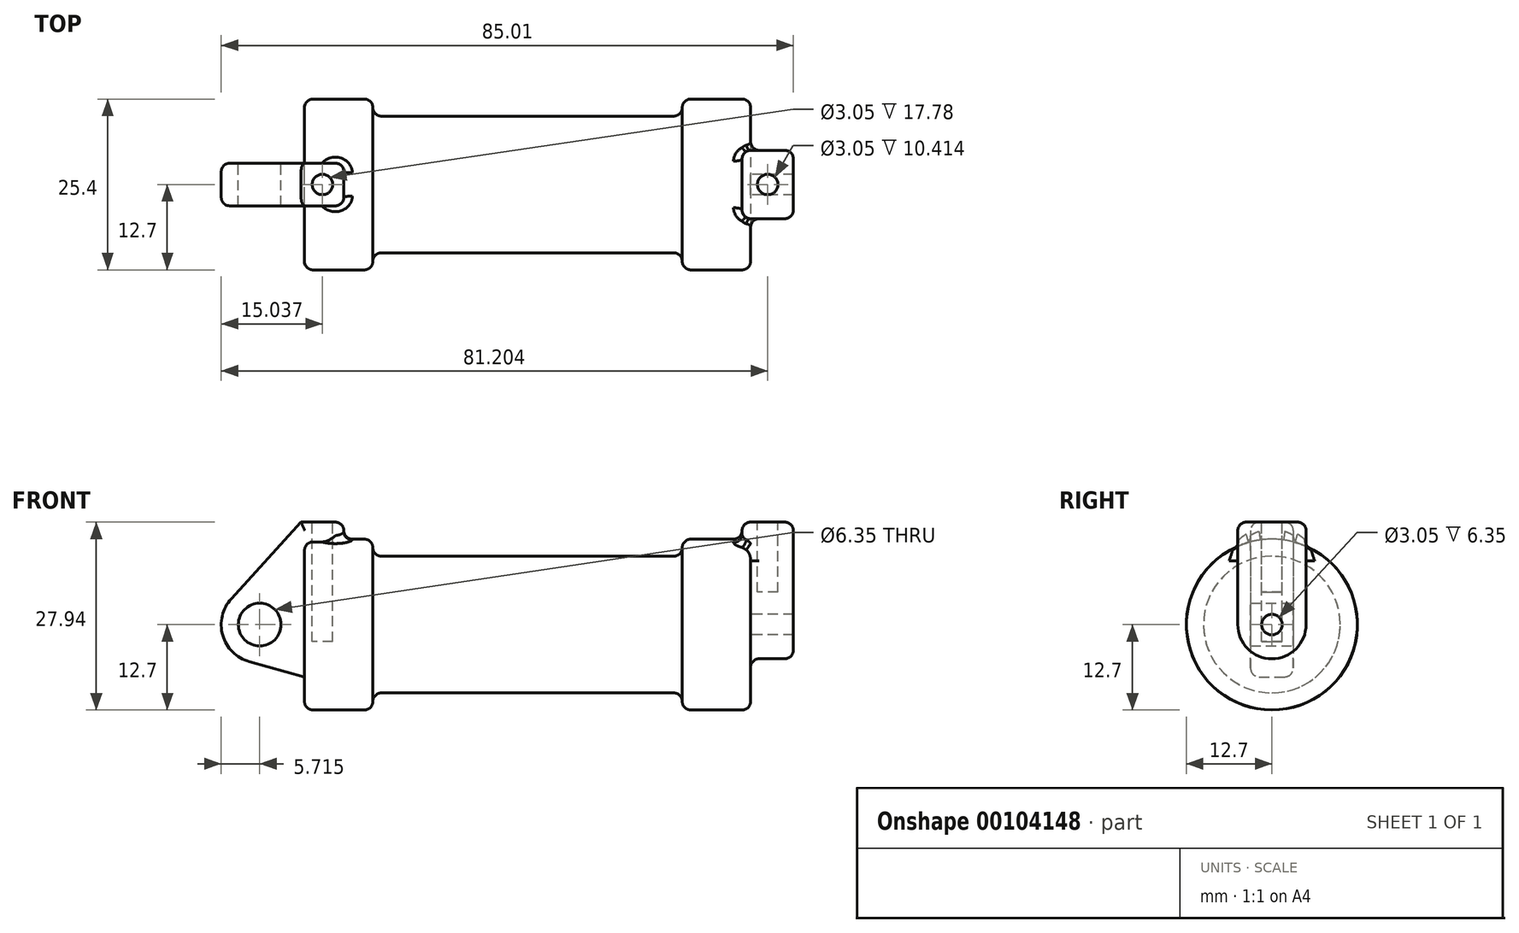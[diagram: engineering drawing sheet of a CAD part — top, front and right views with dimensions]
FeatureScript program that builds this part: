
annotation { "Feature Type Name" : "Feature", "Feature Type Description" : "" }
export const myFeature = defineFeature(function(context is Context, id is Id, definition is map)
    precondition{}
    {
        {
            var Q0;
            Q0=qCreatedBy(makeId("Front.planeOp"),FACE);
            var sketch = newSketch(context, id + "F0", { "sketchPlane" : qUnion([Q0])});
            skLineSegment(sketch, "E0", {"start": v(0, 0) * mm, "end": v(0, 12.7) * mm});
            skLineSegment(sketch, "E1", {"start": v(0, 12.7) * mm, "end": v(10.16, 12.7) * mm});
            skLineSegment(sketch, "E2", {"start": v(10.16, 12.7) * mm, "end": v(10.16, 10.16) * mm});
            skLineSegment(sketch, "E3", {"start": v(10.16, 10.16) * mm, "end": v(56.13, 10.16) * mm});
            skLineSegment(sketch, "E4", {"start": v(56.13, 10.16) * mm, "end": v(56.13, 12.7) * mm});
            skLineSegment(sketch, "E5", {"start": v(56.13, 12.7) * mm, "end": v(66.3, 12.7) * mm});
            skLineSegment(sketch, "E6", {"start": v(66.3, 12.7) * mm, "end": v(66.3, 0) * mm});
            skLineSegment(sketch, "E7", {"start": v(66.3, 0) * mm, "end": v(0, 0) * mm});
            skLineSegment(sketch, "E8", {"start": v(5.84, 15.24) * mm, "end": v(-0.5, 15.24) * mm});
            skLineSegment(sketch, "E9", {"start": v(-0.5, 15.24) * mm, "end": v(-10.88, 3.85) * mm});
            skLineSegment(sketch, "E10", {"start": v(0, 0) * mm, "end": v(-6.65, 0) * mm});
            skCircle(sketch, "E11", {"center": v(-6.65, 0) * mm, "radius": 5.72 * mm});
            skCircle(sketch, "E12", {"center": v(-6.65, 0) * mm, "radius": 3.18 * mm});
            skLineSegment(sketch, "E13", {"start": v(5.84, 15.24) * mm, "end": v(5.84, -9.4) * mm});
            skLineSegment(sketch, "E14", {"start": v(5.84, -9.4) * mm, "end": v(-8.18, -5.5) * mm});
            skSolve(sketch);
        }
        {
            var Q0;
            {var subQ0=sQuery(id+"F0.wireOp",EDGE,"E2");Q0=makeQuery(id+"F0.imprint","IMPRINT",FACE,{"disambiguationData":[TD([[makeQuery(id+"F0.imprint","IMPRINT",EDGE,{"derivedFrom":subQ0}),-1.0]])]});}
            var Q1;
            {var subQ0=sQuery(id+"F0.wireOp",EDGE,"E0");Q1=makeQuery(id+"F0.imprint","IMPRINT",FACE,{"disambiguationData":[TD([[makeQuery(id+"F0.imprint","IMPRINT",EDGE,{"derivedFrom":subQ0}),-1.0]])]});}
            var Q2;
            Q2=sQuery(id+"F0.wireOp",EDGE,"E7");
            revolve(context, id + "F1", {"entities" : qUnion([Q0, Q1]), "axis" : qUnion([Q2]), "revolveType" : RevolveType.FULL});
        }
        {
            var Q0;
            {var subQ0=sQuery(id+"F0.wireOp",EDGE,"E0");Q0=makeQuery(id+"F0.imprint","IMPRINT",FACE,{"disambiguationData":[TD([[makeQuery(id+"F0.imprint","IMPRINT",EDGE,{"derivedFrom":subQ0}),-1.0]])]});}
            var Q1;
            {var subQ3=sQuery(id+"F0.wireOp",EDGE,"E0");Q1=makeQuery(id+"F0.imprint","IMPRINT",FACE,{"disambiguationData":[TD([[makeQuery(id+"F0.imprint","IMPRINT",EDGE,{"derivedFrom":subQ3}),1.0]])]});}
            var Q2;
            {var subQ4=sQuery(id+"F0.wireOp",EDGE,"E12");Q2=makeQuery(id+"F0.imprint","IMPRINT",FACE,{"disambiguationData":[TD([[makeQuery(id+"F0.imprint","IMPRINT",EDGE,{"derivedFrom":subQ4}),-1.0]])]});}
            var Q3;
            {var subQ0=sQuery(id+"F0.wireOp",EDGE,"E14");Q3=makeQuery(id+"F0.imprint","IMPRINT",FACE,{"disambiguationData":[TD([[makeQuery(id+"F0.imprint","IMPRINT",EDGE,{"derivedFrom":subQ0}),-1.0]])]});}
            extrude(context, id + "F2", {"entities" : qUnion([Q0, Q1, Q2, Q3]), "operationType" : NewBodyOperationType.ADD, "endBound" : BoundingType.SYMMETRIC, "depth" : 6.35 * mm});
        }
        {
            var Q0;
            Q0=makeQuery(id+"F1.opRevolve","SWEPT_FACE",FACE,{"disambiguationData":[OSD([sQuery(id+"F0.wireOp",EDGE,"E6")])]});
            var sketch = newSketch(context, id + "F3", { "sketchPlane" : qUnion([Q0])});
            skCircle(sketch, "E15", {"center": v(0, 0) * mm, "radius": 1.52 * mm});
            skCircle(sketch, "E16", {"center": v(0, 0) * mm, "radius": 5.08 * mm});
            skLineSegment(sketch, "E17", {"start": v(5.08, 0) * mm, "end": v(5.08, 15.24) * mm});
            skLineSegment(sketch, "E18", {"start": v(-5.08, 0) * mm, "end": v(-5.08, 15.24) * mm});
            skLineSegment(sketch, "E19", {"start": v(-5.08, 15.24) * mm, "end": v(5.08, 15.24) * mm});
            skSolve(sketch);
        }
        {
            var Q0;
            Q0 = qSketchRegion(id + "F3", true);
            extrude(context, id + "F4", {"entities" : qUnion([Q0]), "operationType" : NewBodyOperationType.ADD, "depth" : 6.35 * mm});
        }
        {
            var Q0;
            Q0 = qSketchRegion(id + "F3", true);
            extrude(context, id + "F5", {"entities" : qUnion([Q0]), "operationType" : NewBodyOperationType.ADD, "oppositeDirection" : true, "depth" : 1.27 * mm});
        }
        {
            var Q0;
            {var subQ0=sQuery(id+"F3.wireOp",EDGE,"E19");Q0=makeQuery(id+"F5.boolean.opBoolean","MERGE",FACE,{"derivedFrom":[makeQuery(id+"F4.opExtrude","SWEPT_FACE",FACE,{"disambiguationData":[OSD([subQ0])]}),makeQuery(id+"F5.opExtrude","SWEPT_FACE",FACE,{"disambiguationData":[OSD([subQ0])]})]});}
            var sketch = newSketch(context, id + "F6", { "sketchPlane" : qUnion([Q0])});
            skCircle(sketch, "E20", {"center": v(68.83, 0) * mm, "radius": 1.52 * mm});
            skLineSegment(sketch, "E21", {"start": v(68.83, 5.08) * mm, "end": v(68.83, 1.52) * mm});
            skLineSegment(sketch, "E22", {"start": v(65.02, 0) * mm, "end": v(67.31, 0) * mm});
            skLineSegment(sketch, "E23.trimOffspring", {"start": v(68.83, -1.52) * mm, "end": v(68.83, -5.08) * mm});
            skLineSegment(sketch, "E24.trimOffspring", {"start": v(70.36, 0) * mm, "end": v(72.64, 0) * mm});
            skSolve(sketch);
        }
        {
            var Q0;
            Q0=makeQuery(id+"F2.opExtrude","SWEPT_FACE",FACE,{"disambiguationData":[OSD([sQuery(id+"F0.wireOp",EDGE,"E8")])]});
            var sketch = newSketch(context, id + "F7", { "sketchPlane" : qUnion([Q0])});
            skCircle(sketch, "E25", {"center": v(2.67, 0) * mm, "radius": 1.52 * mm});
            skLineSegment(sketch, "E26", {"start": v(5.84, 0) * mm, "end": v(4.2, 0) * mm});
            skLineSegment(sketch, "E27", {"start": v(2.67, 3.18) * mm, "end": v(2.67, 1.52) * mm});
            skLineSegment(sketch, "E28.trimOffspring", {"start": v(2.67, -1.52) * mm, "end": v(2.67, -3.18) * mm});
            skLineSegment(sketch, "E29.trimOffspring", {"start": v(1.14, 0) * mm, "end": v(-0.5, 0) * mm});
            skSolve(sketch);
        }
        {
            var Q0;
            {var subQ0=sQuery(id+"F7.wireOp",EDGE,"E25");var subQ1=makeQuery(id+"F7.imprint","INTERSECT",VERTEX,{"derivedFrom":[subQ0,sQuery(id+"F7.wireOp",EDGE,"E26")]});Q0=makeQuery(id+"F7.imprint","IMPRINT",FACE,{"disambiguationData":[TD([[makeQuery(id+"F7.imprint","IMPRINT",EDGE,{"disambiguationData":[TD([[subQ1,-1.0]])],"derivedFrom":subQ0}),1.0]])]});}
            extrude(context, id + "F8", {"entities" : qUnion([Q0]), "operationType" : NewBodyOperationType.REMOVE, "oppositeDirection" : true, "depth" : 17.78 * mm});
        }
        {
            var Q0;
            {var subQ0=sQuery(id+"F6.wireOp",EDGE,"E20");var subQ1=makeQuery(id+"F6.imprint","INTERSECT",VERTEX,{"derivedFrom":[subQ0,sQuery(id+"F6.wireOp",EDGE,"E21")]});Q0=makeQuery(id+"F6.imprint","IMPRINT",FACE,{"disambiguationData":[TD([[makeQuery(id+"F6.imprint","IMPRINT",EDGE,{"disambiguationData":[TD([[subQ1,1.0]])],"derivedFrom":subQ0}),1.0]])]});}
            extrude(context, id + "F9", {"entities" : qUnion([Q0]), "operationType" : NewBodyOperationType.REMOVE, "oppositeDirection" : true, "depth" : 10.4 * mm});
        }
        {
            var Q0;
            Q0=makeQuery(id+"F1.opRevolve","SWEPT_EDGE",EDGE,{"disambiguationData":[OSD([sQuery(id+"F0.wireOp",EDGE,"E1"),sQuery(id+"F0.wireOp",EDGE,"E2")])]});
            var Q1;
            Q1=makeQuery(id+"F1.opRevolve","SWEPT_EDGE",EDGE,{"disambiguationData":[OSD([sQuery(id+"F0.wireOp",EDGE,"E0"),sQuery(id+"F0.wireOp",EDGE,"E1")])]});
            var Q2;
            Q2=makeQuery(id+"F4.boolean.opBoolean","SPLIT",EDGE,{"disambiguationData":[OD(1.0)],"derivedFrom":makeQuery(id+"F1.opRevolve","SWEPT_EDGE",EDGE,{"disambiguationData":[OSD([sQuery(id+"F0.wireOp",EDGE,"E5"),sQuery(id+"F0.wireOp",EDGE,"E6")])]})});
            var Q3;
            Q3=makeQuery(id+"F1.opRevolve","SWEPT_EDGE",EDGE,{"disambiguationData":[OSD([sQuery(id+"F0.wireOp",EDGE,"E4"),sQuery(id+"F0.wireOp",EDGE,"E5")])]});
            var Q4;
            Q4=makeQuery(id+"F1.opRevolve","SWEPT_EDGE",EDGE,{"disambiguationData":[OSD([sQuery(id+"F0.wireOp",EDGE,"E2"),sQuery(id+"F0.wireOp",EDGE,"E3")])]});
            var Q5;
            Q5=makeQuery(id+"F1.opRevolve","SWEPT_EDGE",EDGE,{"disambiguationData":[OSD([sQuery(id+"F0.wireOp",EDGE,"E3"),sQuery(id+"F0.wireOp",EDGE,"E4")])]});
            fillet(context, id + "F10", {"entities" : qUnion([Q0, Q1, Q2, Q3, Q4, Q5]), "radius" : 1.27 * mm, "tangentPropagation" : true, "allowEdgeOverflow" : false});
        }
        {
            var Q0;
            Q0=makeQuery(id+"F2.opExtrude","CAP_EDGE",EDGE,{"disambiguationData":[OSD([sQuery(id+"F0.wireOp",EDGE,"E9")])],"isStart":false});
            var Q1;
            Q1=makeQuery(id+"F2.opExtrude","CAP_EDGE",EDGE,{"disambiguationData":[OSD([sQuery(id+"F0.wireOp",EDGE,"E9")])],"isStart":true});
            var Q2;
            Q2=makeQuery(id+"F2.opExtrude","CAP_EDGE",EDGE,{"disambiguationData":[OSD([sQuery(id+"F0.wireOp",EDGE,"E8")])],"isStart":true});
            var Q3;
            Q3=makeQuery(id+"F2.opExtrude","CAP_EDGE",EDGE,{"disambiguationData":[OSD([sQuery(id+"F0.wireOp",EDGE,"E8")])],"isStart":false});
            var Q4;
            Q4=makeQuery(id+"F2.opExtrude","CAP_EDGE",EDGE,{"disambiguationData":[OSD([sQuery(id+"F0.wireOp",EDGE,"E13")])],"isStart":false});
            var Q5;
            Q5=makeQuery(id+"F2.opExtrude","SWEPT_EDGE",EDGE,{"disambiguationData":[OSD([sQuery(id+"F0.wireOp",EDGE,"E8"),sQuery(id+"F0.wireOp",EDGE,"E13")])]});
            var Q6;
            Q6=makeQuery(id+"F2.opExtrude","CAP_EDGE",EDGE,{"disambiguationData":[OSD([sQuery(id+"F0.wireOp",EDGE,"E13")])],"isStart":true});
            var Q7;
            Q7=makeQuery(id+"F2.opExtrude","CAP_EDGE",EDGE,{"disambiguationData":[OSD([sQuery(id+"F0.wireOp",EDGE,"E11")])],"isStart":false});
            var Q8;
            Q8=makeQuery(id+"F2.opExtrude","CAP_EDGE",EDGE,{"disambiguationData":[OSD([sQuery(id+"F0.wireOp",EDGE,"E14")])],"isStart":false});
            var Q9;
            Q9=makeQuery(id+"F2.opExtrude","CAP_EDGE",EDGE,{"disambiguationData":[OSD([sQuery(id+"F0.wireOp",EDGE,"E14")])],"isStart":true});
            var Q10;
            Q10=makeQuery(id+"F2.opExtrude","CAP_EDGE",EDGE,{"disambiguationData":[OSD([sQuery(id+"F0.wireOp",EDGE,"E11")])],"isStart":true});
            var Q11;
            Q11=makeQuery(id+"F2.boolean.opBoolean","INTERSECT",EDGE,{"derivedFrom":[makeQuery(id+"F1.opRevolve","SWEPT_FACE",FACE,{"disambiguationData":[OSD([sQuery(id+"F0.wireOp",EDGE,"E1")])]}),makeQuery(id+"F2.opExtrude","SWEPT_FACE",FACE,{"disambiguationData":[OSD([sQuery(id+"F0.wireOp",EDGE,"E13")])]})]});
            fillet(context, id + "F11", {"entities" : qUnion([Q0, Q1, Q2, Q3, Q4, Q5, Q6, Q7, Q8, Q9, Q10, Q11]), "radius" : 1.27 * mm, "tangentPropagation" : true, "allowEdgeOverflow" : false});
        }
        {
            var Q0;
            {var subQ0=sQuery(id+"F3.wireOp",EDGE,"E19");var subQ1=sQuery(id+"F3.wireOp",EDGE,"E17");Q0=makeQuery(id+"F5.boolean.opBoolean","MERGE",EDGE,{"derivedFrom":[makeQuery(id+"F4.opExtrude","SWEPT_EDGE",EDGE,{"disambiguationData":[OSD([subQ1,subQ0])]}),makeQuery(id+"F5.opExtrude","SWEPT_EDGE",EDGE,{"disambiguationData":[OSD([subQ1,subQ0])]})]});}
            var Q1;
            Q1=makeQuery(id+"F4.opExtrude","CAP_EDGE",EDGE,{"disambiguationData":[OSD([sQuery(id+"F3.wireOp",EDGE,"E17")])],"isStart":false});
            var Q2;
            {var subQ0=sQuery(id+"F3.wireOp",EDGE,"E19");var subQ1=sQuery(id+"F3.wireOp",EDGE,"E18");Q2=makeQuery(id+"F5.boolean.opBoolean","MERGE",EDGE,{"derivedFrom":[makeQuery(id+"F4.opExtrude","SWEPT_EDGE",EDGE,{"disambiguationData":[OSD([subQ1,subQ0])]}),makeQuery(id+"F5.opExtrude","SWEPT_EDGE",EDGE,{"disambiguationData":[OSD([subQ1,subQ0])]})]});}
            var Q3;
            Q3=makeQuery(id+"F4.opExtrude","CAP_EDGE",EDGE,{"disambiguationData":[OSD([sQuery(id+"F3.wireOp",EDGE,"E19")])],"isStart":false});
            var Q4;
            Q4=makeQuery(id+"F4.opExtrude","CAP_EDGE",EDGE,{"disambiguationData":[OSD([sQuery(id+"F3.wireOp",EDGE,"E18")])],"isStart":false});
            var Q5;
            Q5=makeQuery(id+"F4.opExtrude","CAP_EDGE",EDGE,{"disambiguationData":[OSD([sQuery(id+"F3.wireOp",EDGE,"E16")])],"isStart":false});
            var Q6;
            Q6=makeQuery(id+"F5.opExtrude","CAP_EDGE",EDGE,{"disambiguationData":[OSD([sQuery(id+"F3.wireOp",EDGE,"E19")])],"isStart":false});
            var Q7;
            Q7=makeQuery(id+"F5.opExtrude","CAP_EDGE",EDGE,{"disambiguationData":[OSD([sQuery(id+"F3.wireOp",EDGE,"E17")])],"isStart":false});
            var Q8;
            Q8=makeQuery(id+"F5.opExtrude","CAP_EDGE",EDGE,{"disambiguationData":[OSD([sQuery(id+"F3.wireOp",EDGE,"E18")])],"isStart":false});
            fillet(context, id + "F12", {"entities" : qUnion([Q0, Q1, Q2, Q3, Q4, Q5, Q6, Q7, Q8]), "radius" : 1.27 * mm, "tangentPropagation" : true, "allowEdgeOverflow" : false});
        }
        {
            var Q0;
            Q0=makeQuery(id+"F5.boolean.opBoolean","INTERSECT",EDGE,{"derivedFrom":[makeQuery(id+"F1.opRevolve","SWEPT_FACE",FACE,{"disambiguationData":[OSD([sQuery(id+"F0.wireOp",EDGE,"E5")])]}),makeQuery(id+"F5.opExtrude","CAP_FACE",FACE,{"disambiguationData":[OSD([sQuery(id+"F3.wireOp",EDGE,"E15"),sQuery(id+"F3.wireOp",EDGE,"E16"),sQuery(id+"F3.wireOp",EDGE,"E17"),sQuery(id+"F3.wireOp",EDGE,"E18"),sQuery(id+"F3.wireOp",EDGE,"E19")])],"isStart":false})]});
            fillet(context, id + "F13", {"entities" : qUnion([Q0]), "radius" : 1.27 * mm, "tangentPropagation" : true, "allowEdgeOverflow" : false});
        }
    });
